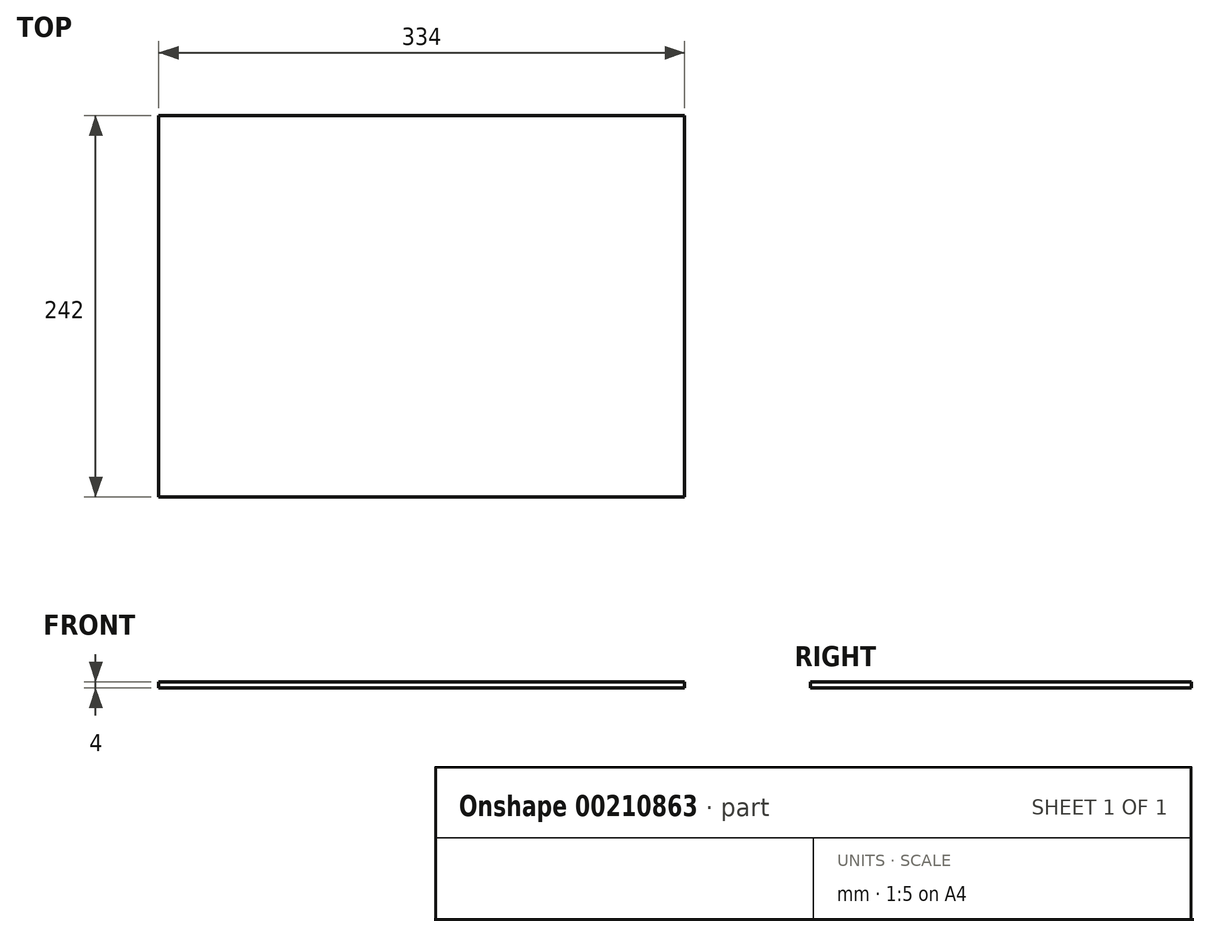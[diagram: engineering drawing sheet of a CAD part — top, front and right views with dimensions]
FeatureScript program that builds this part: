
annotation { "Feature Type Name" : "Feature", "Feature Type Description" : "" }
export const myFeature = defineFeature(function(context is Context, id is Id, definition is map)
    precondition{}
    {
        {
            var Q0;
            Q0=qCreatedBy(makeId("Top.planeOp"),FACE);
            var sketch = newSketch(context, id + "F0", { "sketchPlane" : qUnion([Q0])});
            skLineSegment(sketch, "E0.bottom", {"start": v(167, 121) * mm, "end": v(-167, 121) * mm});
            skLineSegment(sketch, "E0.top", {"start": v(167, -121) * mm, "end": v(-167, -121) * mm});
            skLineSegment(sketch, "E0.left", {"start": v(167, 121) * mm, "end": v(167, -121) * mm});
            skLineSegment(sketch, "E0.right", {"start": v(-167, 121) * mm, "end": v(-167, -121) * mm});
            skPoint(sketch, "E0.middle", {"position": v(0, 0) * mm});
            skSolve(sketch);
        }
        {
            var Q0;
            Q0 = qSketchRegion(id + "F0", true);
            extrude(context, id + "F1", {"entities" : qUnion([Q0]), "depth" : 4 * mm});
        }
    });
